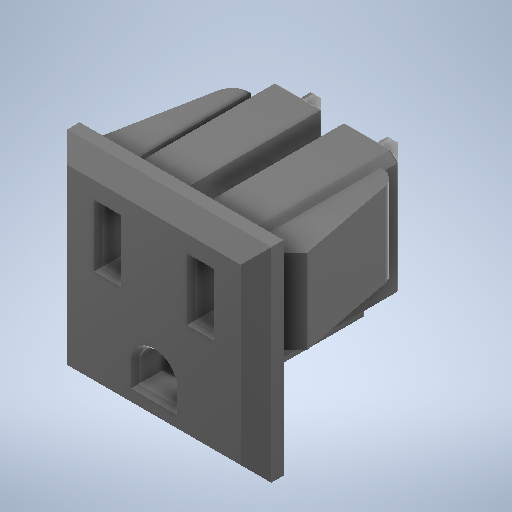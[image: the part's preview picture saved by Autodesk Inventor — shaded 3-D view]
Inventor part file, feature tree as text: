
AUTODESK INVENTOR PART (.ipt)
format: ipt  version: 2025 (Build 290162000, 162)  size: 445,952 bytes
history: native  units: in
note: dims shown in document units (in); Inventor stores cm internally (conversion verified against a paired STEP export)
features: extrude x5, sketch x5, chamfer x4, other x3, projected_geometry x3, mirror x2, fillet x1
ambient origin geometry x8: Origin, YZ Plane, XZ Plane, XY Plane, X Axis, Y Axis, Z Axis, Center Point
bodies: Solid1 (feature_tree)
feature tree (23):
  extrude  "Extrusion1"  Depth=1.0472in
  chamfer  "Chamfer1"  Distance=0.1417in
  extrude  "Extrusion2"  Depth=0.2362in
  extrude  "Extrusion3"  Depth=0.0984in
  chamfer  "Chamfer2"  Distance=0.0984in
  fillet  "Fillet1"  Radius=0.1969in
  other  "XYPlane"
  extrude  "Extrusion4"  Depth=0.1969in
  other  "YZPlane"
  mirror  "Mirror1"
  other  "LeftLine"
  extrude  "Extrusion5"  Depth=0.1181in
  chamfer  "Chamfer3"  Distance=0.1417in
  mirror  "Mirror2"
  chamfer  "Chamfer4"  Distance=0.6693in
  sketch  "Sketch1"  dims[d0=1.0472in d1=1.0472in d2=0.1417in d3=0.0in]
  sketch  "Sketch2"  dims[d4=0.0787in d5=0.0787in d6=45.0deg d7=0.2362in]
  sketch  "Sketch3"  dims[d9=0.185in d11=0.0984in]
  projected_geometry  "Projected Loop1"
  sketch  "Sketch4"  dims[d12=0.2795in]
  projected_geometry  "Projected Loop2"
  projected_geometry  "Projected Loop3"
  sketch  "Sketch5"  dims[d13=0.1575in d14=0.0984in d15=0.1969in d16=0.1969in d17=0.1181in d18=0.1417in d19=0.0in d20=0.6693in d21=0.8465in d22=0.1732in d23=0.2362in d24=0.1732in d25=0.2362in d26=0.1181in d27=0.7874in d28=0.0in d29=0.0394in d30=0.0787in d31=45.0deg d32=0.0197in d33=0.0984in d34=0.1969in d35=0.1181in d36=0.063in d37=0.0787in d38=0.2874in d39=0.1437in d40=0.0in d41=0.0in d42=0.0394in d43=0.1969in d44=0.1181in d45=0.0138in d46=0.0in d47=0.0394in d48=0.0787in d49=45.0deg d50=0.0197in d51=0.0787in d52=45.0deg]
